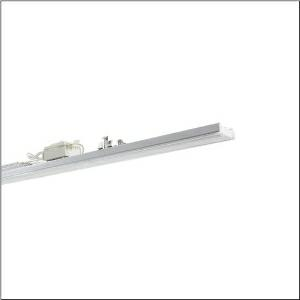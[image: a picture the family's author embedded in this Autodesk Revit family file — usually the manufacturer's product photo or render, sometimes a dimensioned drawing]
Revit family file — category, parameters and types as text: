
# Revit family: licross_r__21_recessed_ho_52te12dn4fxm3s_1d6f
name_source: partatom
category: Lighting Fixtures
units: mm (PartAtom-declared; Revit-internal decimal feet)

## family parameters
Cut with Voids When Loaded = No
Host = Face
Light Source = No
Part Type = Normal
Room Calculation Point = No
Round Connector Dimension = Use Diameter
Shared = No

## types (1)
- --- (1 x LED, 930 lm, 7.5 W, 4000K)
    Apparent Load = 8 VA
    CIE Flux Codes = 69 91 98 100 100
    Color Rendering = 80
    Color Temperature = 4000K
    Default Elevation = 1800 mm
    Description = Licross® 21 Recessed HO, luminaire insert, of sheet steel, galvanised, coil coated, white, length: 1.500mm, width: 66mm, height: 67mm, LED rated luminous flux: 15.000lm, light colour: 840, control gear: DALI 2 (for two DALI lines), with plug, 6-pole, with phase selection, for trunking rail, 14-core, mains connection: 220..240V, AC, 50/60Hz, rated input power: 88W, halogen-free wiring, for emergency light function, for trunking rail, 14-core, converter,control gear: single battery element, battery: LiFePO4, 9Ah, primary optical cover: cover, of PMMA, light emission: direct distribution, primary light characteristic: symmetric, protection rating (complete): IP54, insulation class (complete): insulation class I (protective earthing), certification: CE, UKCA, protection symbol: D if used in an environment with non-conductive dust loads with corresponding accessories, impact resistance: IK06, permissible ambient temperature for indoor applications: +5..+30°C, standard: EN 60598-2-22, LABS conformity tested according to VDMA 24364:2018-05, reducing of maximum allowable ambient temperature of 5°C with ceiling mounting, corresponds to IFS (International Featured Standards) requirements for safety and quality in the food industry, packaging unit: 1 piece
    Height = 58 mm
    Lamp = 1 x LED
    Lamp Light Flux = 930 lm
    Lamp Power = 7.5 W
    Lamp count = 1
    Length = 1500 mm
    Luminous efficacy = 124 lm/W
    Manufacturer = Siteco
    ModVariant = No
    Model = 52TE12DN4FXM3S
    Mounting Place = Ceiling
    Mounting Type = Pendant
    Number of Poles = 1
    OnlyDefault = Yes
    Power Factor = 1
    Product Name = Licross® 21 Recessed HO
    Product group = luminaire insert
    ProductGroupID = 902
    Protection Class = Protection class I
    Protection Degree = IP 54
    RLX_Detail_Level = 1
    RLX_Emergency_Light_Flux = 0 lm
    RLX_Emergency_Type = 0
    RLX_Emergency_Type_DB = No
    RlxData = <blob elided: 25117 chars, md5=d746c017>
    Socket = socket
    Standby Power = 0 W
    System Light Flux = 930 lm
    System Power = 8 W
    Type Comments = : emergency light operation: 3 h
    Type Image = l_1296930.jpg
    URL = http://relux.com
    VarID = @adj_109322
    Voltage = 0 V
    Weight = 0.00 kg
    Width = 66 mm

## geometry (parser evidence)
native form markers: Blend x4, Sweep x13
no freeform markers — native parametric forms only
